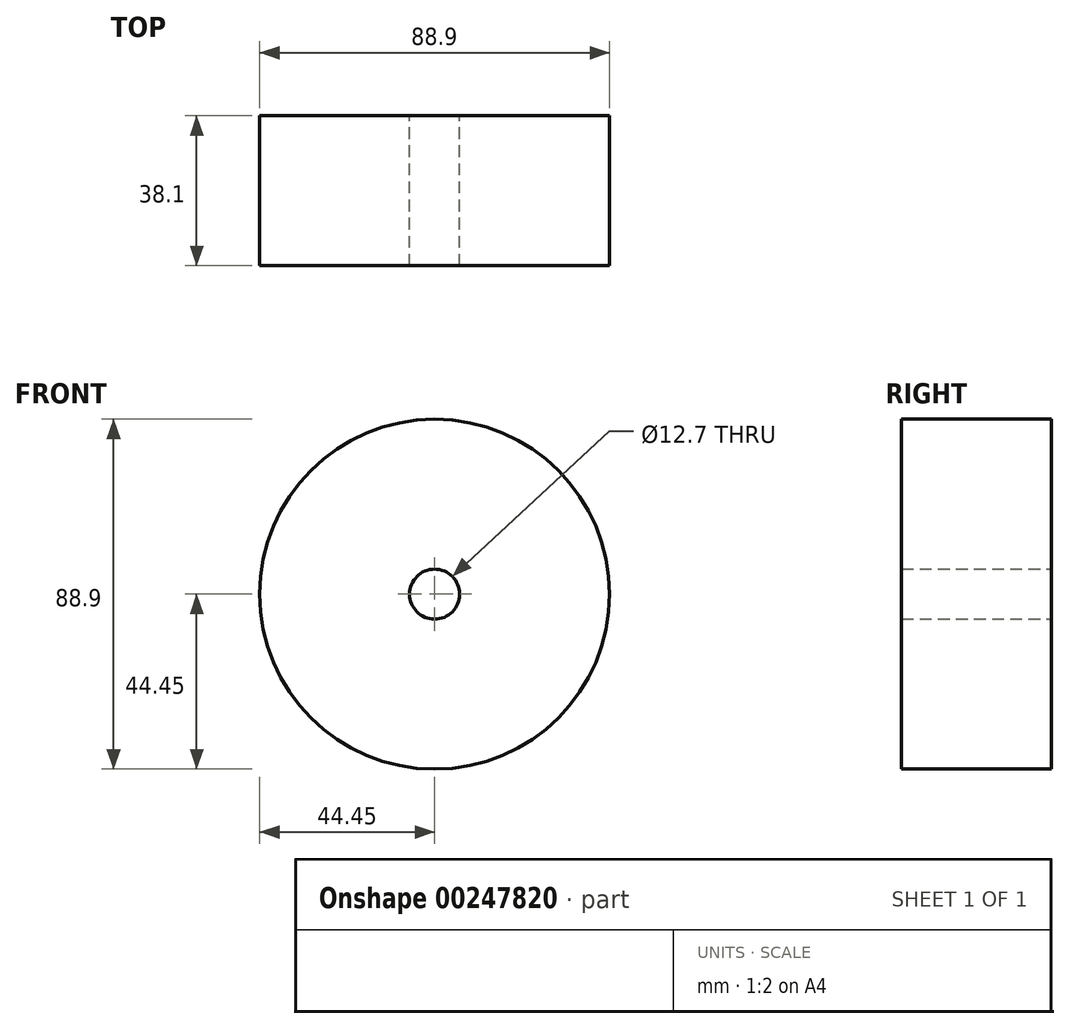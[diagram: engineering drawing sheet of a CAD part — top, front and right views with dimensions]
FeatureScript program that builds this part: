
annotation { "Feature Type Name" : "Feature", "Feature Type Description" : "" }
export const myFeature = defineFeature(function(context is Context, id is Id, definition is map)
    precondition{}
    {
        {
            var Q0;
            Q0=qCreatedBy(makeId("Front.planeOp"),FACE);
            var sketch = newSketch(context, id + "F0", { "sketchPlane" : qUnion([Q0])});
            skCircle(sketch, "E0", {"center": v(0, 0) * mm, "radius": 44.45 * mm});
            skCircle(sketch, "E1", {"center": v(0, 0) * mm, "radius": 6.35 * mm});
            skSolve(sketch);
        }
        {
            var Q0;
            Q0=makeQuery(id+"F0.imprint","IMPRINT",FACE,{"disambiguationData":[TD([[makeQuery(id+"F0.imprint","IMPRINT",EDGE,{"derivedFrom":sQuery(id+"F0.wireOp",EDGE,"E0")}),1.0]])]});
            extrude(context, id + "F1", {"entities" : qUnion([Q0]), "depth" : 38.1 * mm});
        }
    });
